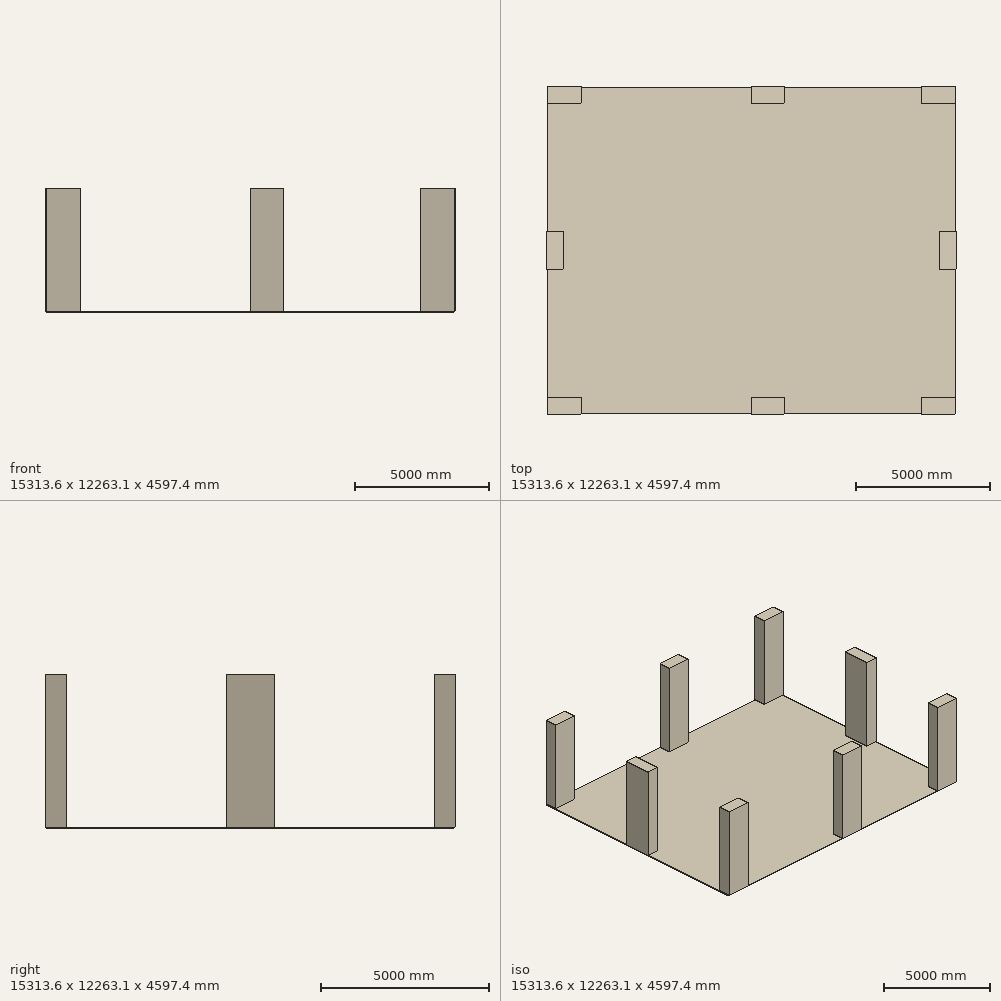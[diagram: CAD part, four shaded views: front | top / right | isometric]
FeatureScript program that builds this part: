
annotation { "Feature Type Name" : "Feature", "Feature Type Description" : "" }
export const myFeature = defineFeature(function(context is Context, id is Id, definition is map)
    precondition{}
    {
        {
            var Q0;
            Q0=qCreatedBy(makeId("Top.planeOp"),FACE);
            var sketch = newSketch(context, id + "F0", { "sketchPlane" : qUnion([Q0])});
            skLineSegment(sketch, "E0.bottom", {"start": v(7620, -6096) * mm, "end": v(-7620, -6096) * mm});
            skLineSegment(sketch, "E0.top", {"start": v(7620, 6096) * mm, "end": v(-7620, 6096) * mm});
            skLineSegment(sketch, "E0.left", {"start": v(7620, -6096) * mm, "end": v(7620, 6096) * mm});
            skLineSegment(sketch, "E0.right", {"start": v(-7620, -6096) * mm, "end": v(-7620, 6096) * mm});
            skPoint(sketch, "E0.middle", {"position": v(0, 0) * mm});
            skSolve(sketch);
        }
        {
            var Q0;
            Q0 = qSketchRegion(id + "F0", true);
            extrude(context, id + "F1", {"entities" : qUnion([Q0]), "depth" : 25.4 * mm});
        }
        {
            var Q0;
            Q0=makeQuery(id+"F1.opExtrude","CAP_FACE",FACE,{"disambiguationData":[OSD([sQuery(id+"F0.wireOp",EDGE,"E0.bottom"),sQuery(id+"F0.wireOp",EDGE,"E0.top"),sQuery(id+"F0.wireOp",EDGE,"E0.left"),sQuery(id+"F0.wireOp",EDGE,"E0.right")])],"isStart":false});
            var sketch = newSketch(context, id + "F2", { "sketchPlane" : qUnion([Q0])});
            skLineSegment(sketch, "E1", {"start": v(0, 6096) * mm, "end": v(0, -6096) * mm, "construction": true});
            skLineSegment(sketch, "E2", {"start": v(-7620, 0) * mm, "end": v(7620, 0) * mm, "construction": true});
            skSolve(sketch);
        }
        {
            var Q0;
            Q0=makeQuery(id+"F2.imprint","IMPRINT",FACE,{"disambiguationData":[TD([[makeQuery(id+"F2.imprint","IMPRINT",EDGE,{"derivedFrom":makeQuery(id+"F1.opExtrude","CAP_EDGE",EDGE,{"disambiguationData":[OSD([sQuery(id+"F0.wireOp",EDGE,"E0.bottom")])],"isStart":false})}),-1.0]])]});
            var sketch = newSketch(context, id + "F3", { "sketchPlane" : qUnion([Q0])});
            skLineSegment(sketch, "E3.bottom", {"start": v(-7612.42, 6131.55) * mm, "end": v(-6364.08, 6131.55) * mm});
            skLineSegment(sketch, "E3.top", {"start": v(-7612.42, 5495.14) * mm, "end": v(-6364.08, 5495.14) * mm});
            skLineSegment(sketch, "E3.left", {"start": v(-7612.42, 6131.55) * mm, "end": v(-7612.42, 5495.14) * mm});
            skLineSegment(sketch, "E3.right", {"start": v(-6364.08, 6131.55) * mm, "end": v(-6364.08, 5495.14) * mm});
            skLineSegment(sketch, "E4.MirrorCS", {"start": v(6364.08, 6131.55) * mm, "end": v(6364.08, 5495.14) * mm});
            skLineSegment(sketch, "E5.MirrorCS", {"start": v(7612.42, 6131.55) * mm, "end": v(6364.08, 6131.55) * mm});
            skLineSegment(sketch, "E6.MirrorCS", {"start": v(7612.42, 6131.55) * mm, "end": v(7612.42, 5495.14) * mm});
            skLineSegment(sketch, "E7.MirrorCS", {"start": v(7612.42, 5495.14) * mm, "end": v(6364.08, 5495.14) * mm});
            skLineSegment(sketch, "E8.MirrorCS", {"start": v(-7612.42, -5495.14) * mm, "end": v(-6364.08, -5495.14) * mm});
            skLineSegment(sketch, "E9.MirrorCS", {"start": v(-7612.42, -6131.55) * mm, "end": v(-7612.42, -5495.14) * mm});
            skLineSegment(sketch, "E10.MirrorCS", {"start": v(-7612.42, -6131.55) * mm, "end": v(-6364.08, -6131.55) * mm});
            skLineSegment(sketch, "E11.MirrorCS", {"start": v(-6364.08, -6131.55) * mm, "end": v(-6364.08, -5495.14) * mm});
            skLineSegment(sketch, "E12.MirrorCS", {"start": v(6364.08, -6131.55) * mm, "end": v(6364.08, -5495.14) * mm});
            skLineSegment(sketch, "E13.MirrorCS", {"start": v(7612.42, -6131.55) * mm, "end": v(6364.08, -6131.55) * mm});
            skLineSegment(sketch, "E14.MirrorCS", {"start": v(7612.42, -6131.55) * mm, "end": v(7612.42, -5495.14) * mm});
            skLineSegment(sketch, "E15.MirrorCS", {"start": v(7612.42, -5495.14) * mm, "end": v(6364.08, -5495.14) * mm});
            skLineSegment(sketch, "E16.MirrorCS", {"start": v(0, 6131.55) * mm, "end": v(0, 5495.14) * mm});
            skLineSegment(sketch, "E17.MirrorCS", {"start": v(1248.34, 5495.14) * mm, "end": v(0, 5495.14) * mm});
            skLineSegment(sketch, "E18.MirrorCS", {"start": v(1248.34, 6131.55) * mm, "end": v(1248.34, 5495.14) * mm});
            skLineSegment(sketch, "E19.MirrorCS", {"start": v(1248.34, 6131.55) * mm, "end": v(0, 6131.55) * mm});
            skLineSegment(sketch, "E20.MirrorCS", {"start": v(0, -6131.55) * mm, "end": v(0, -5495.14) * mm});
            skLineSegment(sketch, "E21.MirrorCS", {"start": v(1248.34, -5495.14) * mm, "end": v(0, -5495.14) * mm});
            skLineSegment(sketch, "E22.MirrorCS", {"start": v(1248.34, -6131.55) * mm, "end": v(1248.34, -5495.14) * mm});
            skLineSegment(sketch, "E23.MirrorCS", {"start": v(1248.34, -6131.55) * mm, "end": v(0, -6131.55) * mm});
            skLineSegment(sketch, "E24.top", {"start": v(-7656.82, 726.29) * mm, "end": v(-7016.7, 726.29) * mm});
            skLineSegment(sketch, "E24.left", {"start": v(-7656.82, 0) * mm, "end": v(-7656.82, 726.29) * mm});
            skLineSegment(sketch, "E24.right", {"start": v(-7016.7, 0) * mm, "end": v(-7016.7, 726.29) * mm});
            skLineSegment(sketch, "E25.MirrorCS", {"start": v(-7016.7, 0) * mm, "end": v(-7016.7, -726.29) * mm});
            skLineSegment(sketch, "E26.MirrorCS", {"start": v(-7656.82, 0) * mm, "end": v(-7656.82, -726.29) * mm});
            skLineSegment(sketch, "E27.MirrorCS", {"start": v(-7656.82, -726.29) * mm, "end": v(-7016.7, -726.29) * mm});
            skLineSegment(sketch, "E28.MirrorCS", {"start": v(7016.7, 0) * mm, "end": v(7016.7, -726.29) * mm});
            skLineSegment(sketch, "E29.MirrorCS", {"start": v(7656.82, -726.29) * mm, "end": v(7016.7, -726.29) * mm});
            skLineSegment(sketch, "E30.MirrorCS", {"start": v(7016.7, 0) * mm, "end": v(7016.7, 726.29) * mm});
            skLineSegment(sketch, "E31.MirrorCS", {"start": v(7656.82, 0) * mm, "end": v(7656.82, -726.29) * mm});
            skLineSegment(sketch, "E32.MirrorCS", {"start": v(7656.82, 726.29) * mm, "end": v(7016.7, 726.29) * mm});
            skLineSegment(sketch, "E33.MirrorCS", {"start": v(7656.82, 0) * mm, "end": v(7656.82, 726.29) * mm});
            skSolve(sketch);
        }
        {
            var Q0;
            Q0 = qSketchRegion(id + "F3", true);
            extrude(context, id + "F4", {"entities" : qUnion([Q0]), "operationType" : NewBodyOperationType.ADD, "depth" : 4572 * mm});
        }
    });
